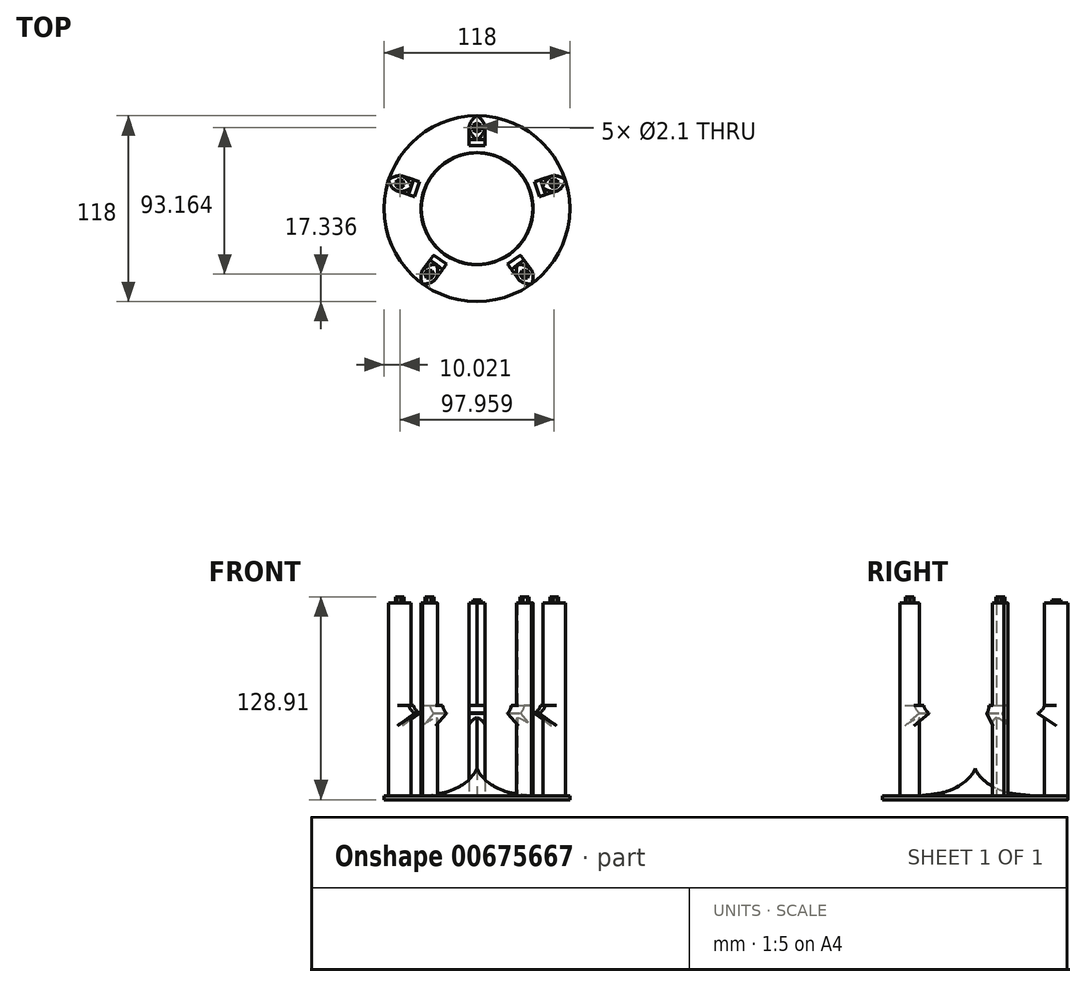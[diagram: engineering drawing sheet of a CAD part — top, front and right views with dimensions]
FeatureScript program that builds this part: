
annotation { "Feature Type Name" : "Feature", "Feature Type Description" : "" }
export const myFeature = defineFeature(function(context is Context, id is Id, definition is map)
    precondition{}
    {
        {
            var Q0;
            Q0=qCreatedBy(makeId("Top.planeOp"),FACE);
            var sketch = newSketch(context, id + "F0", { "sketchPlane" : qUnion([Q0])});
            skCircle(sketch, "E0", {"center": v(0, 0) * mm, "radius": 59 * mm});
            skCircle(sketch, "E1", {"center": v(0, 0) * mm, "radius": 44 * mm});
            skSolve(sketch);
        }
        {
            var Q0;
            Q0=makeQuery(id+"F0.imprint","IMPRINT",FACE,{"disambiguationData":[TD([[makeQuery(id+"F0.imprint","IMPRINT",EDGE,{"derivedFrom":sQuery(id+"F0.wireOp",EDGE,"E0")}),1.0]])]});
            var Q1;
            Q1=makeQuery(id+"F0.imprint","IMPRINT",FACE,{"disambiguationData":[TD([[makeQuery(id+"F0.imprint","IMPRINT",EDGE,{"derivedFrom":sQuery(id+"F0.wireOp",EDGE,"E1")}),1.0]])]});
            extrude(context, id + "F1", {"entities" : qUnion([Q0, Q1]), "depth" : 2.5 * mm, "offsetDistance" : 25 * mm});
        }
        {
            var Q0;
            Q0=makeQuery(id+"F1.opExtrude","CAP_FACE",FACE,{"disambiguationData":[OSD([sQuery(id+"F0.wireOp",EDGE,"E0"),sQuery(id+"F0.wireOp",EDGE,"E1")])],"isStart":false});
            var sketch = newSketch(context, id + "F2", { "sketchPlane" : qUnion([Q0])});
            skFitSpline(sketch, "E2", {"points": [v(0, 59) * mm, v(5, 51.5) * mm, v(0, 44) * mm], "startDerivative": vector(9, -3.6) * mm, "endDerivative": vector(-9, -3.6) * mm});
            skFitSpline(sketch, "E3", {"points": [v(0, 44) * mm, v(-5, 51.5) * mm, v(0, 59) * mm], "startDerivative": vector(-9, 3.6) * mm, "endDerivative": vector(9, 3.6) * mm});
            skLineSegment(sketch, "E4", {"start": v(-5, 51.5) * mm, "end": v(5, 51.5) * mm});
            skLineSegment(sketch, "E5", {"start": v(5, 51.5) * mm, "end": v(5, 33) * mm});
            skLineSegment(sketch, "E6", {"start": v(5, 33) * mm, "end": v(-5, 33) * mm});
            skLineSegment(sketch, "E7", {"start": v(-5, 51.5) * mm, "end": v(-5, 33) * mm});
            skCircle(sketch, "E8", {"center": v(0, 0) * mm, "radius": 44 * mm});
            skSolve(sketch);
        }
        {
            var Q0;
            {var subQ3=sQuery(id+"F2.wireOp",EDGE,"E4");Q0=makeQuery(id+"F2.imprint","IMPRINT",FACE,{"disambiguationData":[TD([[makeQuery(id+"F2.imprint","IMPRINT",EDGE,{"derivedFrom":subQ3}),-1.0]])]});}
            var Q1;
            {var subQ3=sQuery(id+"F2.wireOp",EDGE,"E4");Q1=makeQuery(id+"F2.imprint","IMPRINT",FACE,{"disambiguationData":[TD([[makeQuery(id+"F2.imprint","IMPRINT",EDGE,{"derivedFrom":subQ3}),1.0]])]});}
            extrude(context, id + "F3", {"entities" : qUnion([Q0, Q1]), "operationType" : NewBodyOperationType.ADD, "depth" : 52.4 * mm, "offsetDistance" : 25 * mm});
        }
        {
            var Q0;
            Q0=makeQuery(id+"F3.opExtrude","CAP_FACE",FACE,{"disambiguationData":[OSD([sQuery(id+"F2.wireOp",EDGE,"E2"),sQuery(id+"F2.wireOp",EDGE,"E3")])],"isStart":false});
            var sketch = newSketch(context, id + "F4", { "sketchPlane" : qUnion([Q0])});
            skFitSpline(sketch, "E9", {"points": [v(0, 59) * mm, v(5, 51.5) * mm, v(0, 44) * mm], "startDerivative": vector(9, -3.6) * mm, "endDerivative": vector(-9, -3.6) * mm});
            skFitSpline(sketch, "E10", {"points": [v(0, 44) * mm, v(-5, 51.5) * mm, v(0, 59) * mm], "startDerivative": vector(-9, 3.6) * mm, "endDerivative": vector(9, 3.6) * mm});
            skLineSegment(sketch, "E11", {"start": v(-5, 51.5) * mm, "end": v(5, 51.5) * mm});
            skLineSegment(sketch, "E12", {"start": v(5, 51.5) * mm, "end": v(5, 40) * mm});
            skLineSegment(sketch, "E13", {"start": v(5, 40) * mm, "end": v(-5, 40) * mm});
            skLineSegment(sketch, "E14", {"start": v(-5, 51.5) * mm, "end": v(-5, 40) * mm});
            skCircle(sketch, "E15", {"center": v(0, 0) * mm, "radius": 44 * mm});
            skSolve(sketch);
        }
        {
            var Q0;
            {var subQ5=sQuery(id+"F4.wireOp",EDGE,"E13");Q0=makeQuery(id+"F4.imprint","IMPRINT",FACE,{"disambiguationData":[TD([[makeQuery(id+"F4.imprint","IMPRINT",EDGE,{"derivedFrom":subQ5}),-1.0]])]});}
            var Q1;
            {var subQ0=sQuery(id+"F4.wireOp",EDGE,"E15");var subQ3=sQuery(id+"F4.wireOp",EDGE,"E12");var subQ5=makeQuery(id+"F4.imprint","INTERSECT",VERTEX,{"derivedFrom":[subQ3,subQ0]});Q1=makeQuery(id+"F4.imprint","IMPRINT",FACE,{"disambiguationData":[TD([[makeQuery(id+"F4.imprint","IMPRINT",EDGE,{"disambiguationData":[TD([[subQ5,1.0]])],"derivedFrom":subQ3}),-1.0]])]});}
            var Q2;
            {var subQ0=sQuery(id+"F4.wireOp",EDGE,"E15");var subQ3=sQuery(id+"F4.wireOp",EDGE,"E14");var subQ5=makeQuery(id+"F4.imprint","INTERSECT",VERTEX,{"derivedFrom":[subQ3,subQ0]});Q2=makeQuery(id+"F4.imprint","IMPRINT",FACE,{"disambiguationData":[TD([[makeQuery(id+"F4.imprint","IMPRINT",EDGE,{"disambiguationData":[TD([[subQ5,1.0]])],"derivedFrom":subQ3}),1.0]])]});}
            var Q3;
            {var subQ3=sQuery(id+"F4.wireOp",EDGE,"E11");Q3=makeQuery(id+"F4.imprint","IMPRINT",FACE,{"disambiguationData":[TD([[makeQuery(id+"F4.imprint","IMPRINT",EDGE,{"derivedFrom":subQ3}),-1.0]])]});}
            extrude(context, id + "F5", {"entities" : qUnion([Q0, Q1, Q2, Q3]), "operationType" : NewBodyOperationType.ADD, "depth" : 0.1 * mm, "offsetDistance" : 25 * mm});
        }
        {
            var Q0;
            Q0=makeQuery(id+"F5.opExtrude","SWEPT_FACE",FACE,{"disambiguationData":[OSD([sQuery(id+"F4.wireOp",EDGE,"E14")])]});
            var sketch = newSketch(context, id + "F6", { "sketchPlane" : qUnion([Q0])});
            skLineSegment(sketch, "E16", {"start": v(-51.5, 55.01) * mm, "end": v(-51.5, 0) * mm});
            skLineSegment(sketch, "E17", {"start": v(-40, 54.91) * mm, "end": v(-51.5, 47.01) * mm});
            skSolve(sketch);
        }
        {
            var Q0;
            {var subQ2=sQuery(id+"F6.wireOp",EDGE,"E17");Q0=makeQuery(id+"F6.imprint","IMPRINT",FACE,{"disambiguationData":[TD([[makeQuery(id+"F6.imprint","IMPRINT",EDGE,{"derivedFrom":subQ2}),-1.0]])]});}
            extrude(context, id + "F7", {"entities" : qUnion([Q0]), "operationType" : NewBodyOperationType.ADD, "depth" : -10 * mm, "offsetDistance" : 25 * mm});
        }
        {
            var Q0;
            Q0=makeQuery(id+"F5.opExtrude","SWEPT_FACE",FACE,{"disambiguationData":[OSD([sQuery(id+"F4.wireOp",EDGE,"E14")])]});
            var sketch = newSketch(context, id + "F8", { "sketchPlane" : qUnion([Q0])});
            skLineSegment(sketch, "E18", {"start": v(-51.5, 60) * mm, "end": v(-51.5, 55.01) * mm});
            skLineSegment(sketch, "E19", {"start": v(-51.5, 60) * mm, "end": v(-44, 60) * mm});
            skFitSpline(sketch, "E20", {"points": [v(-44, 60) * mm, v(-43.7, 58.92) * mm, v(-42.5, 57) * mm, v(-40, 55.01) * mm], "startDerivative": vector(2.06, -8.41) * mm, "endDerivative": vector(4.98, -1.95) * mm});
            skSolve(sketch);
        }
        {
            var Q0;
            Q0=makeQuery(id+"F8.imprint","IMPRINT",FACE,{"disambiguationData":[TD([[makeQuery(id+"F8.imprint","IMPRINT",EDGE,{"derivedFrom":sQuery(id+"F8.wireOp",EDGE,"E18")}),1.0]])]});
            extrude(context, id + "F9", {"entities" : qUnion([Q0]), "operationType" : NewBodyOperationType.ADD, "depth" : -10 * mm, "offsetDistance" : 25 * mm});
        }
        {
            var Q0;
            Q0=makeQuery(id+"F3.opExtrude","CAP_FACE",FACE,{"disambiguationData":[OSD([sQuery(id+"F2.wireOp",EDGE,"E2"),sQuery(id+"F2.wireOp",EDGE,"E3")])],"isStart":false});
            var sketch = newSketch(context, id + "F10", { "sketchPlane" : qUnion([Q0])});
            skFitSpline(sketch, "E21", {"points": [v(0, 59) * mm, v(5, 51.5) * mm, v(0, 44) * mm], "startDerivative": vector(9, -3.6) * mm, "endDerivative": vector(-9, -3.6) * mm});
            skFitSpline(sketch, "E22", {"points": [v(0, 44) * mm, v(-5, 51.5) * mm, v(0, 59) * mm], "startDerivative": vector(-9, 3.6) * mm, "endDerivative": vector(9, 3.6) * mm});
            skSolve(sketch);
        }
        {
            var Q0;
            Q0=makeQuery(id+"F10.imprint","IMPRINT",FACE,{"disambiguationData":[TD([[makeQuery(id+"F10.imprint","IMPRINT",EDGE,{"derivedFrom":sQuery(id+"F10.wireOp",EDGE,"E21")}),-1.0]])]});
            extrude(context, id + "F11", {"entities" : qUnion([Q0]), "operationType" : NewBodyOperationType.ADD, "depth" : 70 * mm, "offsetDistance" : 25 * mm});
        }
        {
            var Q0;
            Q0=makeQuery(id+"F11.opExtrude","CAP_FACE",FACE,{"disambiguationData":[OSD([sQuery(id+"F10.wireOp",EDGE,"E21"),sQuery(id+"F10.wireOp",EDGE,"E22")])],"isStart":false});
            var sketch = newSketch(context, id + "F12", { "sketchPlane" : qUnion([Q0])});
            skCircle(sketch, "E23", {"center": v(0, 51.5) * mm, "radius": 2.9 * mm});
            skLineSegment(sketch, "E24", {"start": v(0, 15) * mm, "end": v(0, 59) * mm});
            skLineSegment(sketch, "E25", {"start": v(0, 54.4) * mm, "end": v(2.51, 52.95) * mm});
            skLineSegment(sketch, "E26", {"start": v(0, 48.6) * mm, "end": v(2.51, 50.05) * mm});
            skLineSegment(sketch, "E27", {"start": v(2.51, 52.95) * mm, "end": v(2.51, 50.05) * mm});
            skLineSegment(sketch, "E28", {"start": v(0, 54.4) * mm, "end": v(-2.51, 52.95) * mm});
            skLineSegment(sketch, "E29", {"start": v(-2.51, 52.95) * mm, "end": v(-2.51, 50.05) * mm});
            skLineSegment(sketch, "E30", {"start": v(-2.51, 50.05) * mm, "end": v(0, 48.6) * mm});
            skCircle(sketch, "E31", {"center": v(0, 51.5) * mm, "radius": 1.05 * mm});
            skSolve(sketch);
        }
        {
            var Q0;
            {var subQ0=sQuery(id+"F12.wireOp",EDGE,"E28");Q0=makeQuery(id+"F12.imprint","IMPRINT",FACE,{"disambiguationData":[TD([[makeQuery(id+"F12.imprint","IMPRINT",EDGE,{"derivedFrom":subQ0}),1.0]])]});}
            var Q1;
            {var subQ0=sQuery(id+"F12.wireOp",EDGE,"E25");Q1=makeQuery(id+"F12.imprint","IMPRINT",FACE,{"disambiguationData":[TD([[makeQuery(id+"F12.imprint","IMPRINT",EDGE,{"derivedFrom":subQ0}),-1.0]])]});}
            extrude(context, id + "F13", {"entities" : qUnion([Q0, Q1]), "depth" : 4 * mm, "offsetDistance" : 25 * mm});
        }
        {
            var Q0;
            Q0=qCreatedBy(makeId("Right.planeOp"),FACE);
            var sketch = newSketch(context, id + "F14", { "sketchPlane" : qUnion([Q0])});
            skLineSegment(sketch, "E32", {"start": v(0, 0) * mm, "end": v(-44, 4.03) * mm});
            skLineSegment(sketch, "E33", {"start": v(0, 0) * mm, "end": v(0, 19.95) * mm});
            skLineSegment(sketch, "E34", {"start": v(35.5, 2.5) * mm, "end": v(0, 2.5) * mm});
            skFitSpline(sketch, "E35", {"points": [v(35.5, 2.5) * mm, v(26.22, 3.5) * mm, v(18.5, 5.05) * mm, v(12.03, 7.9) * mm, v(6.85, 11.2) * mm, v(2.4, 15.6) * mm, v(0, 19.95) * mm], "startDerivative": vector(-68.57, 8.12) * mm, "endDerivative": vector(-13.37, 35.14) * mm});
            skSolve(sketch);
        }
        {
            var Q0;
            {var subQ2=sQuery(id+"F14.wireOp",EDGE,"E34");Q0=makeQuery(id+"F14.imprint","IMPRINT",FACE,{"disambiguationData":[TD([[makeQuery(id+"F14.imprint","IMPRINT",EDGE,{"derivedFrom":subQ2}),-1.0]])]});}
            var Q1;
            Q1=makeQuery(id+"F1.opExtrude","SWEPT_FACE",FACE,{"disambiguationData":[OSD([sQuery(id+"F0.wireOp",EDGE,"E0")])]});
            revolve(context, id + "F15", {"operationType" : NewBodyOperationType.ADD, "entities" : qUnion([Q0]), "axis" : qUnion([Q1]), "revolveType" : RevolveType.FULL});
        }
        {
            var Q0;
            Q0=makeQuery(id+"F11.opExtrude","SWEPT_BODY",BODY,{"disambiguationData":[OSD([sQuery(id+"F10.wireOp",EDGE,"E21"),sQuery(id+"F10.wireOp",EDGE,"E22")])]});
            var Q1;
            Q1=makeQuery(id+"F1.opExtrude","SWEPT_BODY",BODY,{"disambiguationData":[OSD([sQuery(id+"F0.wireOp",EDGE,"E0")])]});
            var Q2;
            Q2=makeQuery(id+"F7.opExtrude","SWEPT_BODY",BODY,{"disambiguationData":[OSD([sQuery(id+"F4.wireOp",EDGE,"E14"),sQuery(id+"F6.wireOp",EDGE,"E16"),sQuery(id+"F6.wireOp",EDGE,"E17")])]});
            var Q3;
            Q3=makeQuery(id+"F9.opExtrude","SWEPT_BODY",BODY,{"disambiguationData":[OSD([sQuery(id+"F4.wireOp",EDGE,"E14"),sQuery(id+"F8.wireOp",EDGE,"E18"),sQuery(id+"F8.wireOp",EDGE,"E19"),sQuery(id+"F8.wireOp",EDGE,"E20")])]});
            var Q4;
            Q4=makeQuery(id+"F13.opExtrude","SWEPT_BODY",BODY,{"disambiguationData":[OSD([sQuery(id+"F12.wireOp",EDGE,"E23")])]});
            var Q5;
            Q5=makeQuery(id+"F13.opExtrude","SWEPT_BODY",BODY,{"disambiguationData":[OSD([sQuery(id+"F12.wireOp",EDGE,"E25"),sQuery(id+"F12.wireOp",EDGE,"E26"),sQuery(id+"F12.wireOp",EDGE,"E27"),sQuery(id+"F12.wireOp",EDGE,"E28"),sQuery(id+"F12.wireOp",EDGE,"E29"),sQuery(id+"F12.wireOp",EDGE,"E30"),sQuery(id+"F12.wireOp",EDGE,"E31")])]});
            var Q6;
            Q6=makeQuery(id+"F1.opExtrude","CAP_EDGE",EDGE,{"disambiguationData":[OSD([sQuery(id+"F0.wireOp",EDGE,"E0")])],"isStart":true});
            circularPattern(context, id + "F16", {"entities" : qUnion([Q0, Q1, Q2, Q3, Q4, Q5]), "axis" : qUnion([Q6]), "angle" : 360 * degree, "instanceCount" : 5, "equalSpace" : true});
        }
        {
            var Q0;
            Q0=makeQuery(id+"F13.opExtrude","CAP_FACE",FACE,{"disambiguationData":[OSD([sQuery(id+"F12.wireOp",EDGE,"E25"),sQuery(id+"F12.wireOp",EDGE,"E26"),sQuery(id+"F12.wireOp",EDGE,"E27"),sQuery(id+"F12.wireOp",EDGE,"E28"),sQuery(id+"F12.wireOp",EDGE,"E29"),sQuery(id+"F12.wireOp",EDGE,"E30"),sQuery(id+"F12.wireOp",EDGE,"E31")])],"isStart":false});
            var sketch = newSketch(context, id + "F17", { "sketchPlane" : qUnion([Q0])});
            skCircle(sketch, "E36", {"center": v(0, 51.5) * mm, "radius": 2.9 * mm});
            skSolve(sketch);
        }
        {
            var Q0;
            Q0=makeQuery(id+"F17.imprint","IMPRINT",FACE,{"disambiguationData":[TD([[makeQuery(id+"F17.imprint","IMPRINT",EDGE,{"derivedFrom":sQuery(id+"F17.wireOp",EDGE,"E36")}),1.0]])]});
            var Q1;
            Q1=makeQuery(id+"F17.imprint","IMPRINT",FACE,{"disambiguationData":[TD([[makeQuery(id+"F17.imprint","IMPRINT",EDGE,{"derivedFrom":makeQuery(id+"F13.opExtrude","CAP_EDGE",EDGE,{"disambiguationData":[OSD([sQuery(id+"F12.wireOp",EDGE,"E25")])],"isStart":false})}),-1.0]])]});
            extrude(context, id + "F18", {"entities" : qUnion([Q0, Q1]), "operationType" : NewBodyOperationType.REMOVE, "oppositeDirection" : true, "depth" : 2 * mm, "offsetDistance" : 25 * mm});
        }
    });
